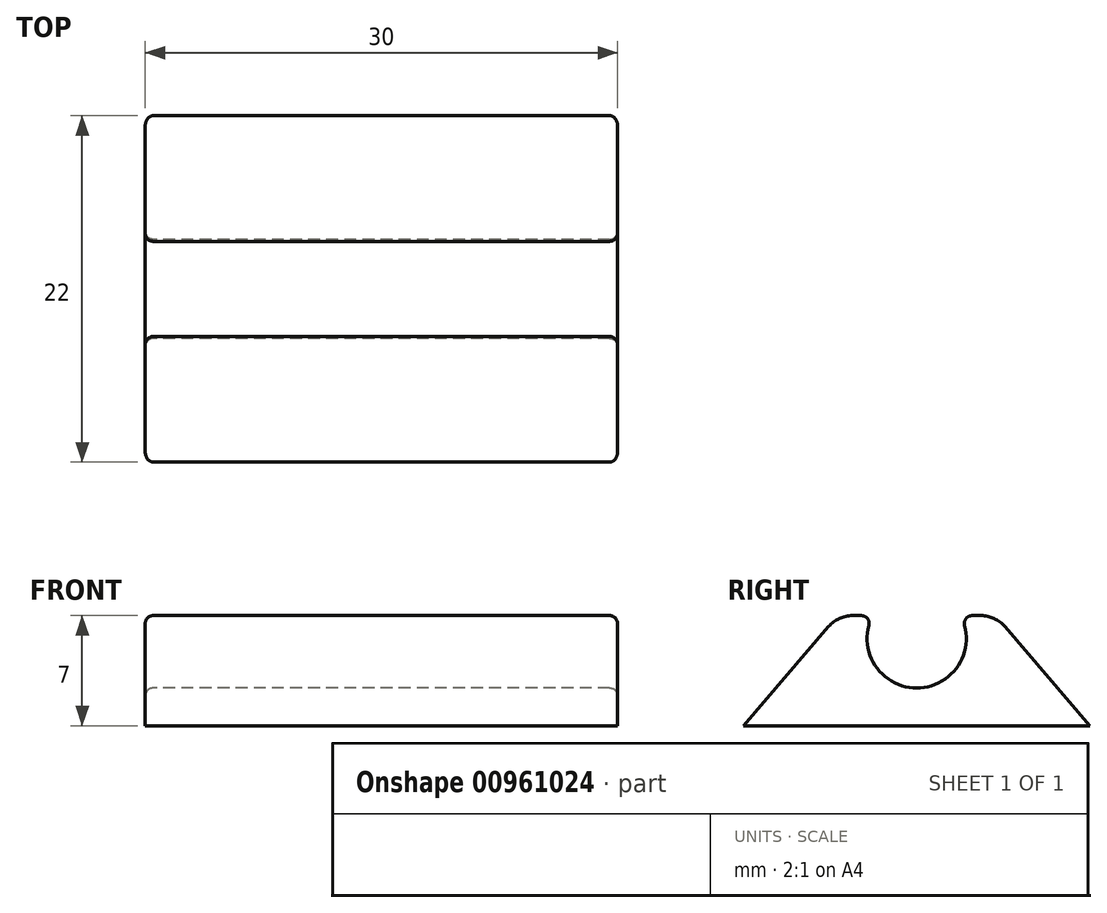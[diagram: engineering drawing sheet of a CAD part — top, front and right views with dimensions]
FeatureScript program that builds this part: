
annotation { "Feature Type Name" : "Feature", "Feature Type Description" : "" }
export const myFeature = defineFeature(function(context is Context, id is Id, definition is map)
    precondition{}
    {
        {
            var Q0;
            Q0=qCreatedBy(makeId("Top.planeOp"),FACE);
            var sketch = newSketch(context, id + "F0", { "sketchPlane" : qUnion([Q0])});
            skLineSegment(sketch, "E0.bottom", {"start": v(15, -5) * mm, "end": v(-15, -5) * mm});
            skLineSegment(sketch, "E0.top", {"start": v(15, 5) * mm, "end": v(-15, 5) * mm});
            skLineSegment(sketch, "E0.left", {"start": v(15, -5) * mm, "end": v(15, 5) * mm});
            skLineSegment(sketch, "E0.right", {"start": v(-15, -5) * mm, "end": v(-15, 5) * mm});
            skPoint(sketch, "E0.middle", {"position": v(0, 0) * mm});
            skSolve(sketch);
        }
        {
            var Q0;
            Q0 = qSketchRegion(id + "F0", true);
            extrude(context, id + "F1", {"entities" : qUnion([Q0]), "flatOperationType" : FlatOperationType.REMOVE, "depth" : 7 * mm, "offsetDistance" : 25 * mm, "domain" : OperationDomain.MODEL});
        }
        {
            var Q0;
            Q0=makeQuery(id+"F1.opExtrude","SWEPT_FACE",FACE,{"disambiguationData":[OSD([sQuery(id+"F0.wireOp",EDGE,"E0.right")])]});
            var sketch = newSketch(context, id + "F2", { "sketchPlane" : qUnion([Q0]), "disableImprinting" : false});
            skCircle(sketch, "E1", {"center": v(0, 5.55) * mm, "radius": 3.15 * mm});
            skLineSegment(sketch, "E2", {"start": v(0, 0) * mm, "end": v(0, 14.52) * mm, "construction": true});
            skSolve(sketch);
        }
        {
            var Q0;
            Q0 = qSketchRegion(id + "F2", true);
            extrude(context, id + "F3", {"entities" : qUnion([Q0]), "operationType" : NewBodyOperationType.REMOVE, "endBound" : BoundingType.THROUGH_ALL, "oppositeDirection" : true, "depth" : 25 * mm, "offsetDistance" : 25 * mm});
        }
        {
            var Q0;
            Q0=makeQuery(id+"F3.boolean.opBoolean","INTERSECT",EDGE,{"disambiguationData":[OD(0.0)],"derivedFrom":[makeQuery(id+"F1.opExtrude","CAP_FACE",FACE,{"disambiguationData":[OSD([sQuery(id+"F0.wireOp",EDGE,"E0.bottom"),sQuery(id+"F0.wireOp",EDGE,"E0.top"),sQuery(id+"F0.wireOp",EDGE,"E0.left"),sQuery(id+"F0.wireOp",EDGE,"E0.right")])],"isStart":false}),makeQuery(id+"F3.opExtrude","SWEPT_FACE",FACE,{"disambiguationData":[OSD([sQuery(id+"F2.wireOp",EDGE,"E1")])]})]});
            var Q1;
            Q1=makeQuery(id+"F3.boolean.opBoolean","INTERSECT",EDGE,{"disambiguationData":[OD(1.0)],"derivedFrom":[makeQuery(id+"F1.opExtrude","CAP_FACE",FACE,{"disambiguationData":[OSD([sQuery(id+"F0.wireOp",EDGE,"E0.bottom"),sQuery(id+"F0.wireOp",EDGE,"E0.top"),sQuery(id+"F0.wireOp",EDGE,"E0.left"),sQuery(id+"F0.wireOp",EDGE,"E0.right")])],"isStart":false}),makeQuery(id+"F3.opExtrude","SWEPT_FACE",FACE,{"disambiguationData":[OSD([sQuery(id+"F2.wireOp",EDGE,"E1")])]})]});
            var Q2;
            Q2=makeQuery(id+"F3.boolean.opBoolean","INTERSECT",EDGE,{"disambiguationData":[OD(1.0)],"derivedFrom":[makeQuery(id+"F1.opExtrude","CAP_FACE",FACE,{"disambiguationData":[OSD([sQuery(id+"F0.wireOp",EDGE,"E0.bottom"),sQuery(id+"F0.wireOp",EDGE,"E0.top"),sQuery(id+"F0.wireOp",EDGE,"E0.left"),sQuery(id+"F0.wireOp",EDGE,"E0.right")])],"isStart":false}),makeQuery(id+"F3.opExtrude","SWEPT_FACE",FACE,{"disambiguationData":[OSD([sQuery(id+"F2.wireOp",EDGE,"467d7fe5-b6a0-49a0-b0e0-15e039d8215c0.MirrorC")])]})]});
            var Q3;
            Q3=makeQuery(id+"F3.boolean.opBoolean","INTERSECT",EDGE,{"disambiguationData":[OD(0.0)],"derivedFrom":[makeQuery(id+"F1.opExtrude","CAP_FACE",FACE,{"disambiguationData":[OSD([sQuery(id+"F0.wireOp",EDGE,"E0.bottom"),sQuery(id+"F0.wireOp",EDGE,"E0.top"),sQuery(id+"F0.wireOp",EDGE,"E0.left"),sQuery(id+"F0.wireOp",EDGE,"E0.right")])],"isStart":false}),makeQuery(id+"F3.opExtrude","SWEPT_FACE",FACE,{"disambiguationData":[OSD([sQuery(id+"F2.wireOp",EDGE,"467d7fe5-b6a0-49a0-b0e0-15e039d8215c0.MirrorC")])]})]});
            fillet(context, id + "F4", {"entities" : qUnion([Q0, Q1, Q2, Q3]), "radius" : .5 * mm, "tangentPropagation" : true, "allowEdgeOverflow" : false});
        }
        {
            var Q0;
            Q0=makeQuery(id+"F1.opExtrude","SWEPT_FACE",FACE,{"disambiguationData":[OSD([sQuery(id+"F0.wireOp",EDGE,"E0.left")])]});
            var sketch = newSketch(context, id + "F5", { "sketchPlane" : qUnion([Q0])});
            skLineSegment(sketch, "E3", {"start": v(-5, 7) * mm, "end": v(-11, 0) * mm});
            skLineSegment(sketch, "E4", {"start": v(-11, 0) * mm, "end": v(-5, 0) * mm});
            skLineSegment(sketch, "E5", {"start": v(-5, 0) * mm, "end": v(-5, 7) * mm});
            skLineSegment(sketch, "E6", {"start": v(0, 0) * mm, "end": v(0, -2.57) * mm, "construction": true});
            skLineSegment(sketch, "E7.MirrorCS", {"start": v(5, 7) * mm, "end": v(11, 0) * mm});
            skLineSegment(sketch, "E8.MirrorCS", {"start": v(11, 0) * mm, "end": v(5, 0) * mm});
            skLineSegment(sketch, "E9.MirrorCS", {"start": v(5, 0) * mm, "end": v(5, 7) * mm});
            skSolve(sketch);
        }
        {
            var Q0;
            Q0 = qSketchRegion(id + "F5", true);
            var Q1;
            Q1=makeQuery(id+"F1.opExtrude","SWEPT_FACE",FACE,{"disambiguationData":[OSD([sQuery(id+"F0.wireOp",EDGE,"E0.right")])]});
            extrude(context, id + "F6", {"entities" : qUnion([Q0]), "operationType" : NewBodyOperationType.ADD, "endBound" : BoundingType.UP_TO_SURFACE, "oppositeDirection" : true, "depth" : 25 * mm, "endBoundEntityFace" : qUnion([Q1]), "offsetDistance" : 25 * mm});
        }
        {
            var Q0;
            Q0=makeQuery(id+"F6.boolean.opBoolean","MERGE",EDGE,{"derivedFrom":[makeQuery(id+"F1.opExtrude","CAP_EDGE",EDGE,{"disambiguationData":[OSD([sQuery(id+"F0.wireOp",EDGE,"E0.bottom")])],"isStart":false}),makeQuery(id+"F6.opExtrude","SWEPT_EDGE",EDGE,{"disambiguationData":[OSD([sQuery(id+"F0.wireOp",EDGE,"E0.left"),sQuery(id+"F5.wireOp",EDGE,"E3"),sQuery(id+"F5.wireOp",EDGE,"E5")])]})]});
            var Q1;
            Q1=makeQuery(id+"F6.boolean.opBoolean","MERGE",EDGE,{"derivedFrom":[makeQuery(id+"F1.opExtrude","CAP_EDGE",EDGE,{"disambiguationData":[OSD([sQuery(id+"F0.wireOp",EDGE,"E0.top")])],"isStart":false}),makeQuery(id+"F6.opExtrude","SWEPT_EDGE",EDGE,{"disambiguationData":[OSD([sQuery(id+"F0.wireOp",EDGE,"E0.left"),sQuery(id+"F5.wireOp",EDGE,"E7.MirrorCS"),sQuery(id+"F5.wireOp",EDGE,"E9.MirrorCS")])]})]});
            fillet(context, id + "F7", {"entities" : qUnion([Q0, Q1]), "tangentPropagation" : true, "radius" : 2 * mm, "defaultsChanged" : false, "vertexSettings" : [], "allowEdgeOverflow" : false});
        }
        {
            var Q0;
            Q0=makeQuery(id+"F6.opExtrude","CAP_EDGE",EDGE,{"disambiguationData":[OSD([sQuery(id+"F5.wireOp",EDGE,"E3")])],"isStart":true});
            var Q1;
            {var subQ0=sQuery(id+"F0.wireOp",EDGE,"E0.bottom");var subQ1=sQuery(id+"F0.wireOp",EDGE,"E0.left");Q1=makeQuery(id+"F3.boolean.opBoolean","SPLIT",EDGE,{"disambiguationData":[TD([makeQuery(id+"F1.opExtrude","SWEPT_FACE",FACE,{"disambiguationData":[OSD([subQ0])]})])],"derivedFrom":makeQuery(id+"F1.opExtrude","CAP_EDGE",EDGE,{"disambiguationData":[OSD([subQ1])],"isStart":false})});}
            var Q2;
            Q2=makeQuery(id+"F6.opExtrude","CAP_EDGE",EDGE,{"disambiguationData":[OSD([sQuery(id+"F5.wireOp",EDGE,"E7.MirrorCS")])],"isStart":true});
            var Q3;
            Q3=makeQuery(id+"F6.opExtrude","CAP_EDGE",EDGE,{"disambiguationData":[OSD([sQuery(id+"F5.wireOp",EDGE,"E3")])],"isStart":false});
            var Q4;
            {var subQ0=sQuery(id+"F0.wireOp",EDGE,"E0.bottom");var subQ1=sQuery(id+"F0.wireOp",EDGE,"E0.right");Q4=makeQuery(id+"F3.boolean.opBoolean","SPLIT",EDGE,{"disambiguationData":[TD([makeQuery(id+"F1.opExtrude","SWEPT_FACE",FACE,{"disambiguationData":[OSD([subQ0])]})])],"derivedFrom":makeQuery(id+"F1.opExtrude","CAP_EDGE",EDGE,{"disambiguationData":[OSD([subQ1])],"isStart":false})});}
            var Q5;
            Q5=makeQuery(id+"F6.opExtrude","CAP_EDGE",EDGE,{"disambiguationData":[OSD([sQuery(id+"F5.wireOp",EDGE,"E7.MirrorCS")])],"isStart":false});
            fillet(context, id + "F8", {"entities" : qUnion([Q0, Q1, Q2, Q3, Q4, Q5]), "tangentPropagation" : true, "radius" : 0.5 * mm, "defaultsChanged" : false, "vertexSettings" : [], "allowEdgeOverflow" : false});
        }
    });
